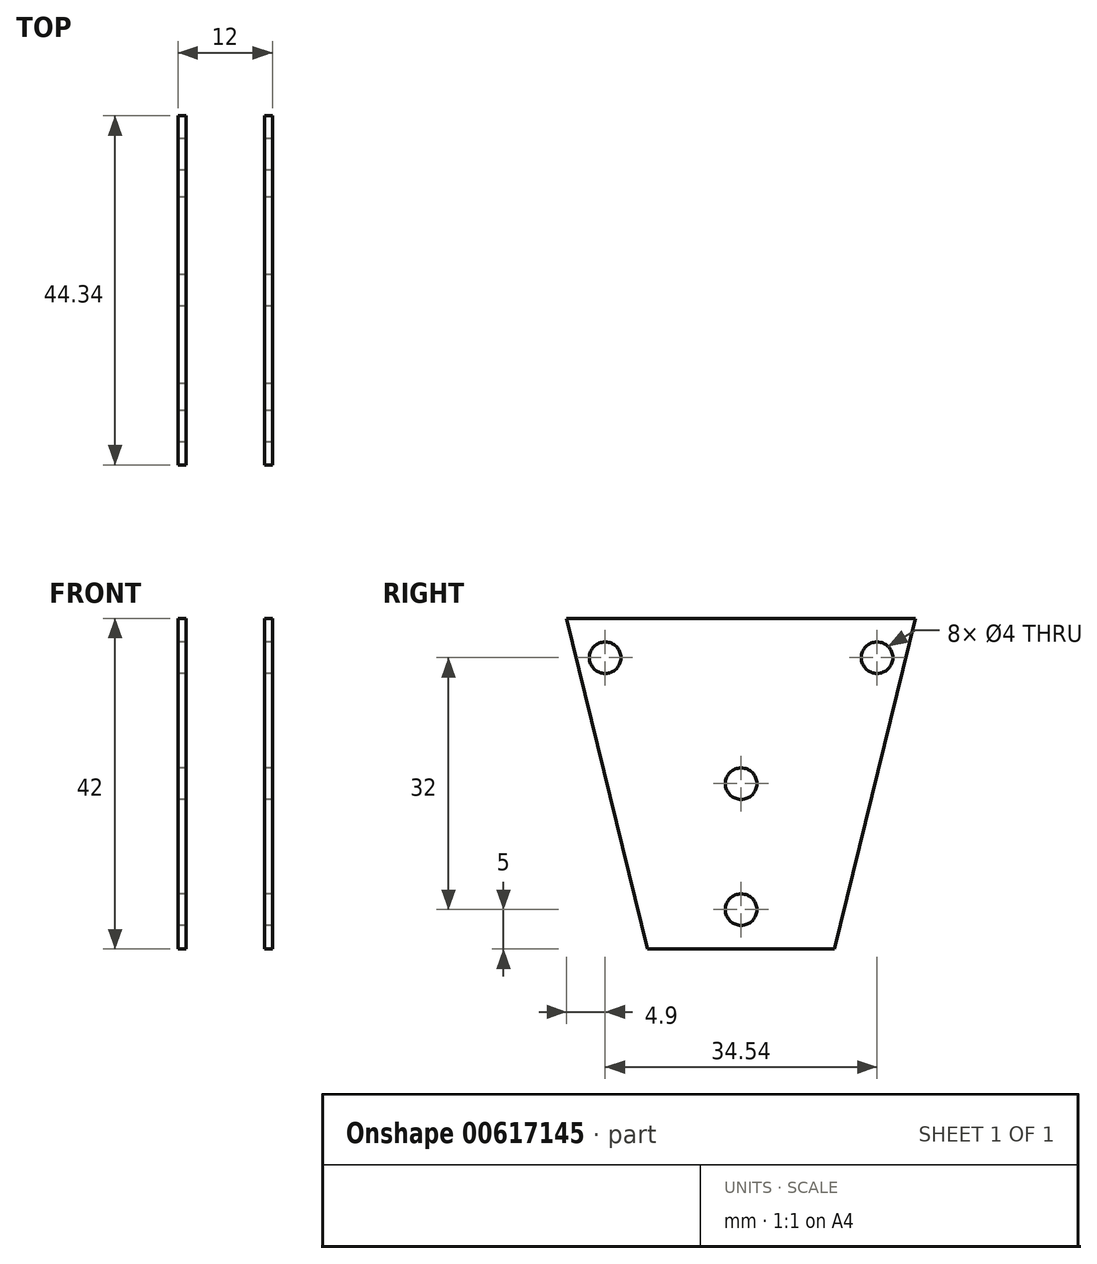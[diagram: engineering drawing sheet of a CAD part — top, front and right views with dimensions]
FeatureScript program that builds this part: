
annotation { "Feature Type Name" : "Feature", "Feature Type Description" : "" }
export const myFeature = defineFeature(function(context is Context, id is Id, definition is map)
    precondition{}
    {
        {
            var Q0;
            Q0=qCreatedBy(makeId("Right.planeOp"),FACE);
            var sketch = newSketch(context, id + "F0", { "sketchPlane" : qUnion([Q0])});
            skLineSegment(sketch, "E0", {"start": v(0, 21) * mm, "end": v(-22.17, 21) * mm});
            skLineSegment(sketch, "E1", {"start": v(-22.17, 21) * mm, "end": v(-11.86, -21) * mm});
            skLineSegment(sketch, "E2", {"start": v(-11.86, -21) * mm, "end": v(0, -21) * mm});
            skCircle(sketch, "E3", {"center": v(0, -16) * mm, "radius": 2 * mm});
            skCircle(sketch, "E4", {"center": v(-17.27, 16) * mm, "radius": 2 * mm});
            skCircle(sketch, "E5", {"center": v(0, 0) * mm, "radius": 2 * mm});
            skLineSegment(sketch, "E6.MirrorCS", {"start": v(11.86, -21) * mm, "end": v(0, -21) * mm});
            skLineSegment(sketch, "E7.MirrorCS", {"start": v(0, 21) * mm, "end": v(22.17, 21) * mm});
            skLineSegment(sketch, "E8.MirrorCS", {"start": v(22.17, 21) * mm, "end": v(11.86, -21) * mm});
            skCircle(sketch, "E9.MirrorC", {"center": v(17.27, 16) * mm, "radius": 2 * mm});
            skSolve(sketch);
        }
        {
            var Q0;
            Q0 = qSketchRegion(id + "F0", true);
            extrude(context, id + "F1", {"entities" : qUnion([Q0]), "endBound" : BoundingType.SYMMETRIC, "depth" : 12 * mm, "offsetDistance" : 25 * mm});
        }
        {
            var Q0;
            Q0=qCreatedBy(makeId("Front.planeOp"),FACE);
            var sketch = newSketch(context, id + "F2", { "sketchPlane" : qUnion([Q0])});
            skLineSegment(sketch, "E10.bottom", {"start": v(5, -39.25) * mm, "end": v(-5, -39.25) * mm});
            skLineSegment(sketch, "E10.top", {"start": v(5, 39.25) * mm, "end": v(-5, 39.25) * mm});
            skLineSegment(sketch, "E10.left", {"start": v(5, -39.25) * mm, "end": v(5, 39.25) * mm});
            skLineSegment(sketch, "E10.right", {"start": v(-5, -39.25) * mm, "end": v(-5, 39.25) * mm});
            skPoint(sketch, "E10.middle", {"position": v(0, 0) * mm});
            skSolve(sketch);
        }
        {
            var Q0;
            Q0 = qSketchRegion(id + "F2", true);
            extrude(context, id + "F3", {"entities" : qUnion([Q0]), "operationType" : NewBodyOperationType.REMOVE, "endBound" : BoundingType.SYMMETRIC, "oppositeDirection" : true, "depth" : 100 * mm, "offsetDistance" : 25 * mm});
        }
    });
